# Revit family: BSC-Class-II_Type-A2_NuAire_BioSafetyCab_677
name_source: partatom
category: Mechanical Equipment
units: mm (PartAtom-declared; Revit-internal decimal feet)

## family parameters
Always vertical = Yes
Classification Number = 23.40.70.11.11.11.11
Cut with Voids When Loaded = No
Maintain Annotation Orientation = No
Part Type = Normal
Room Calculation Point = No
Round Connector Dimension = Use Diameter
Shared = No
Work Plane-Based = No

## types (3) — shared parameters
Assembly Code = E1020720
Construction Details = http://www.arcat.com
DEPTH = 2' - 7 19/32"
Default Elevation = 0' - 0"
Description = Class II Type A2 Biological Safety Cabinet
HEIGHT = 4' - 10 7/8"
Keynote = 11 53 00
Manufacturer = Nuaire Inc
Manufacturer Fax = 763-553-0459
Manufacturer Website = http://www.nuaire.com
Product Data = http://www.arcat.com
Product Properties = http://www.nuaire.com
Revision = R1_12-2015
Sales Information = http://www.nuaire.com
Specification = http://www.arcat.com
URL = http://www.nuaire.com
WORK SURFACE HEIGHT = 2' - 8 5/8"
zero-valued in all types: Cost

## per-type parameters (varying)
| type | ACCESS HEIGHT | LEG WIDTH | Model | WIDTH |
| 400 - 36" Work Surface Height | 0' - 8 9/32" | 4' - 1 13/16" | NU-677-400 | 4' - 5 13/16" |
| 500 - 36" Work Surface Height | 0' - 8 9/32" | 5' - 1 13/16" | NU-677-500 | 5' - 5 13/16" |
| 600 - 36" Work Surface Height | 1' - 0" | 6' - 1 13/16" | NU-677-600 | 6' - 5 13/16" |

## geometry (parser evidence)
native form markers: Blend x10, Sweep x3
no freeform markers — native parametric forms only
